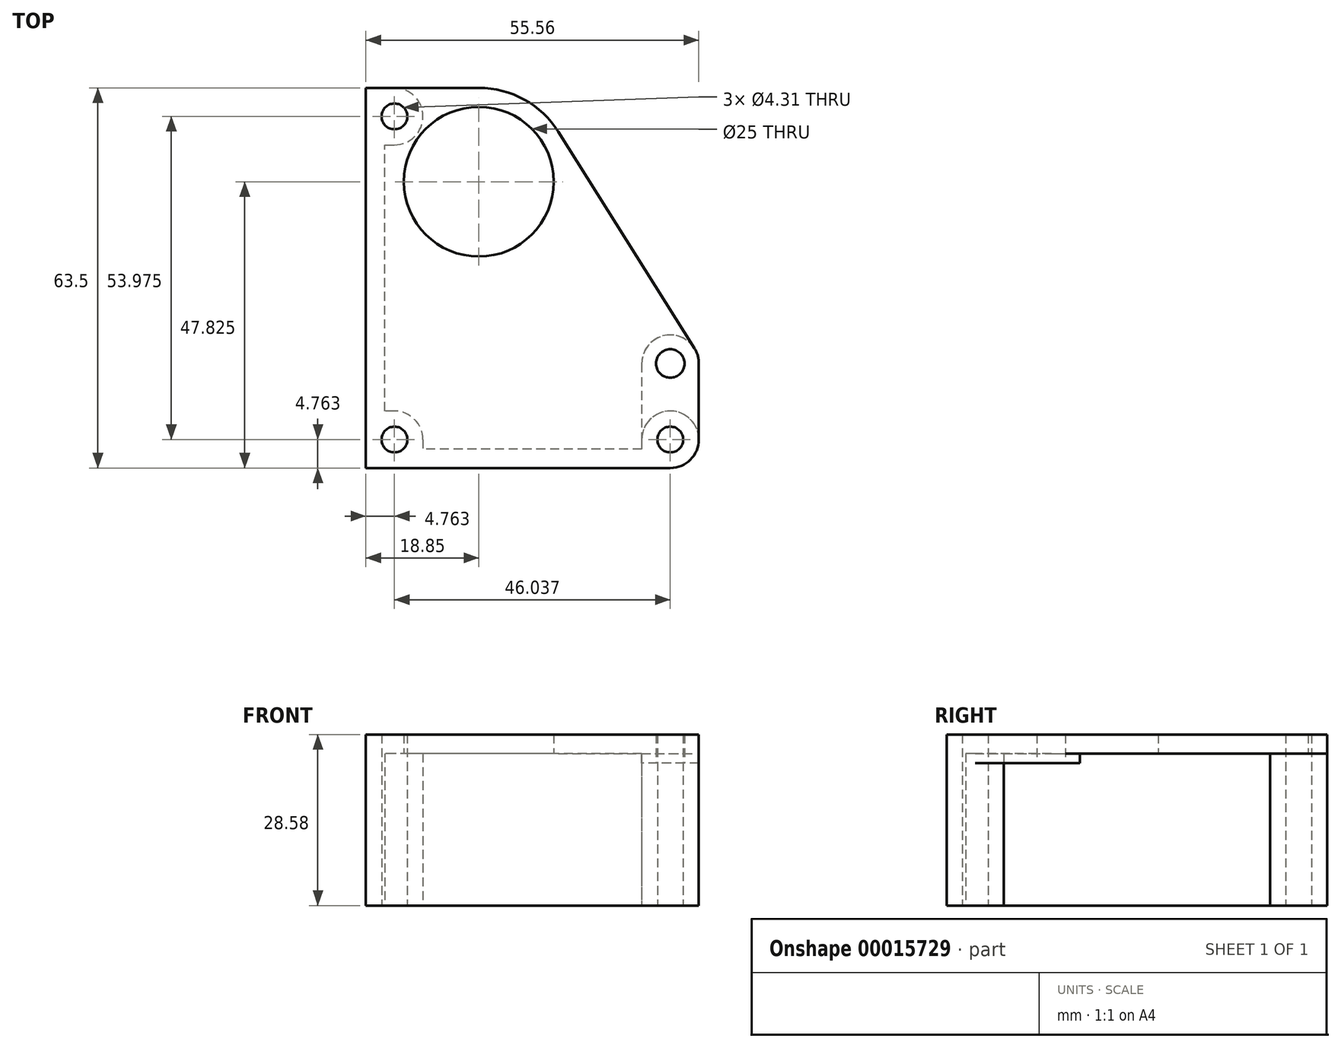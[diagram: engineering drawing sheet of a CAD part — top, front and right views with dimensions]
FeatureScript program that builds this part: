
annotation { "Feature Type Name" : "Feature", "Feature Type Description" : "" }
export const myFeature = defineFeature(function(context is Context, id is Id, definition is map)
    precondition{}
    {
        {
            var Q0;
            Q0=qCreatedBy(makeId("Top.planeOp"),FACE);
            var sketch = newSketch(context, id + "F0", { "sketchPlane" : qUnion([Q0])});
            skLineSegment(sketch, "E0.bottom", {"start": v(0, 0) * mm, "end": v(50.8, 0) * mm});
            skLineSegment(sketch, "E0.left", {"start": v(0, 0) * mm, "end": v(0, 63.5) * mm});
            skLineSegment(sketch, "E1", {"start": v(4.76, 0) * mm, "end": v(4.76, 4.76) * mm, "construction": true});
            skLineSegment(sketch, "E2", {"start": v(4.76, 4.76) * mm, "end": v(0, 4.76) * mm, "construction": true});
            skCircle(sketch, "E3", {"center": v(4.76, 4.76) * mm, "radius": 2.15 * mm});
            skCircle(sketch, "E4", {"center": v(50.8, 4.76) * mm, "radius": 2.15 * mm});
            skArc(sketch, "E5", {"start": v(50.8, 0) * mm, "mid": v(54.17, 8.13) * mm, "end": v(46.04, 4.76) * mm});
            skLineSegment(sketch, "E6", {"start": v(46.04, 4.76) * mm, "end": v(46.04, 3.18) * mm});
            skLineSegment(sketch, "E7", {"start": v(46.04, 3.18) * mm, "end": v(9.53, 3.17) * mm});
            skLineSegment(sketch, "E8", {"start": v(9.53, 4.76) * mm, "end": v(9.53, 3.17) * mm});
            skArc(sketch, "E9", {"start": v(9.53, 4.76) * mm, "mid": v(8.13, 8.13) * mm, "end": v(4.76, 9.52) * mm});
            skLineSegment(sketch, "E10", {"start": v(46.04, 3.18) * mm, "end": v(46.04, 0) * mm, "construction": true});
            skLineSegment(sketch, "E11", {"start": v(4.76, 9.52) * mm, "end": v(3.18, 9.52) * mm});
            skLineSegment(sketch, "E12", {"start": v(3.18, 9.52) * mm, "end": v(3.18, 53.98) * mm});
            skLineSegment(sketch, "E13", {"start": v(0, 63.5) * mm, "end": v(4.76, 63.5) * mm});
            skArc(sketch, "E14", {"start": v(4.76, 53.97) * mm, "mid": v(9.52, 58.74) * mm, "end": v(4.76, 63.5) * mm});
            skLineSegment(sketch, "E15", {"start": v(3.17, 53.98) * mm, "end": v(4.76, 53.98) * mm});
            skCircle(sketch, "E16", {"center": v(4.76, 58.74) * mm, "radius": 2.15 * mm});
            skLineSegment(sketch, "E17", {"start": v(50.8, 4.76) * mm, "end": v(50.8, 22.23) * mm, "construction": true});
            skLineSegment(sketch, "E18", {"start": v(4.76, 58.74) * mm, "end": v(23.08, 58.74) * mm, "construction": true});
            skLineSegment(sketch, "E19", {"start": v(23.08, 58.74) * mm, "end": v(23.08, 49.95) * mm, "construction": true});
            skLineSegment(sketch, "E20", {"start": v(23.08, 49.95) * mm, "end": v(50.8, 22.23) * mm, "construction": true});
            skSolve(sketch);
        }
        {
            var Q0;
            Q0 = qSketchRegion(id + "F0", true);
            extrude(context, id + "F1", {"entities" : qUnion([Q0]), "depth" : 25.4 * mm});
        }
        {
            var Q0;
            Q0=makeQuery(id+"F1.opExtrude","CAP_FACE",FACE,{"disambiguationData":[OSD([sQuery(id+"F0.wireOp",EDGE,"E0.bottom"),sQuery(id+"F0.wireOp",EDGE,"E0.left"),sQuery(id+"F0.wireOp",EDGE,"E3"),sQuery(id+"F0.wireOp",EDGE,"E4"),sQuery(id+"F0.wireOp",EDGE,"E5"),sQuery(id+"F0.wireOp",EDGE,"E6"),sQuery(id+"F0.wireOp",EDGE,"E7"),sQuery(id+"F0.wireOp",EDGE,"E8"),sQuery(id+"F0.wireOp",EDGE,"E9"),sQuery(id+"F0.wireOp",EDGE,"E11"),sQuery(id+"F0.wireOp",EDGE,"E12"),sQuery(id+"F0.wireOp",EDGE,"E13"),sQuery(id+"F0.wireOp",EDGE,"E14"),sQuery(id+"F0.wireOp",EDGE,"E15"),sQuery(id+"F0.wireOp",EDGE,"E16")])],"isStart":false});
            var sketch = newSketch(context, id + "F2", { "sketchPlane" : qUnion([Q0])});
            skLineSegment(sketch, "E21", {"start": v(55.56, 4.76) * mm, "end": v(55.56, 17.46) * mm});
            skLineSegment(sketch, "E22.bottom", {"start": v(50.8, 0) * mm, "end": v(0, 0) * mm});
            skLineSegment(sketch, "E22.top", {"start": v(18.85, 63.5) * mm, "end": v(0, 63.5) * mm});
            skLineSegment(sketch, "E22.right", {"start": v(0, 0) * mm, "end": v(0, 63.5) * mm});
            skArc(sketch, "E23", {"start": v(55.56, 17.46) * mm, "mid": v(55.38, 18.78) * mm, "end": v(54.83, 20) * mm});
            skArc(sketch, "E24", {"start": v(32.13, 56.16) * mm, "mid": v(26.43, 61.54) * mm, "end": v(18.85, 63.5) * mm});
            skCircle(sketch, "E25", {"center": v(18.85, 47.83) * mm, "radius": 12.5 * mm});
            skLineSegment(sketch, "E26", {"start": v(18.85, 47.83) * mm, "end": v(6.35, 47.83) * mm, "construction": true});
            skLineSegment(sketch, "E27", {"start": v(6.35, 47.83) * mm, "end": v(3.18, 47.83) * mm, "construction": true});
            skLineSegment(sketch, "E28", {"start": v(50.8, 4.76) * mm, "end": v(50.8, 17.46) * mm, "construction": true});
            skLineSegment(sketch, "E29", {"start": v(32.13, 56.16) * mm, "end": v(54.83, 20) * mm});
            skCircle(sketch, "E30", {"center": v(4.76, 58.74) * mm, "radius": 2.15 * mm});
            skCircle(sketch, "E31", {"center": v(50.8, 4.76) * mm, "radius": 2.15 * mm});
            skCircle(sketch, "E32", {"center": v(4.76, 4.76) * mm, "radius": 2.15 * mm});
            skCircle(sketch, "E33", {"center": v(50.8, 17.46) * mm, "radius": 2.38 * mm});
            skSolve(sketch);
        }
        {
            var Q0;
            {var subQ1=sQuery(id+"F2.wireOp",EDGE,"E21");Q0=makeQuery(id+"F2.imprint","IMPRINT",FACE,{"disambiguationData":[TD([[makeQuery(id+"F2.imprint","IMPRINT",EDGE,{"derivedFrom":subQ1}),1.0]])]});}
            var Q1;
            {var subQ0=sQuery(id+"F2.wireOp",EDGE,"E22.bottom");Q1=makeQuery(id+"F2.imprint","IMPRINT",FACE,{"disambiguationData":[TD([[makeQuery(id+"F2.imprint","IMPRINT",EDGE,{"derivedFrom":subQ0}),1.0]])]});}
            extrude(context, id + "F3", {"entities" : qUnion([Q0, Q1]), "operationType" : NewBodyOperationType.ADD, "depth" : 3.17 * mm});
        }
        {
            var Q0;
            Q0=makeQuery(id+"F3.opExtrude","CAP_FACE",FACE,{"disambiguationData":[OSD([sQuery(id+"F0.wireOp",EDGE,"E5"),sQuery(id+"F2.wireOp",EDGE,"E21"),sQuery(id+"F2.wireOp",EDGE,"E22.bottom"),sQuery(id+"F2.wireOp",EDGE,"E22.top"),sQuery(id+"F2.wireOp",EDGE,"E22.right"),sQuery(id+"F2.wireOp",EDGE,"E23"),sQuery(id+"F2.wireOp",EDGE,"E24"),sQuery(id+"F2.wireOp",EDGE,"E25"),sQuery(id+"F2.wireOp",EDGE,"E29"),sQuery(id+"F2.wireOp",EDGE,"E30"),sQuery(id+"F2.wireOp",EDGE,"E31"),sQuery(id+"F2.wireOp",EDGE,"E32"),sQuery(id+"F2.wireOp",EDGE,"E33")])],"isStart":true});
            var sketch = newSketch(context, id + "F4", { "sketchPlane" : qUnion([Q0])});
            skArc(sketch, "E34", {"start": v(46.04, -17.46) * mm, "mid": v(50.8, -22.23) * mm, "end": v(55.56, -17.46) * mm});
            skLineSegment(sketch, "E35", {"start": v(55.56, -4.76) * mm, "end": v(55.56, -17.46) * mm});
            skLineSegment(sketch, "E36", {"start": v(46.04, -17.46) * mm, "end": v(46.04, -4.76) * mm});
            skArc(sketch, "E37", {"start": v(46.04, -4.76) * mm, "mid": v(50.8, -9.53) * mm, "end": v(55.56, -4.76) * mm});
            skCircle(sketch, "E38", {"center": v(50.8, -17.46) * mm, "radius": 2.38 * mm});
            skSolve(sketch);
        }
        {
            var Q0;
            Q0 = qSketchRegion(id + "F4", true);
            extrude(context, id + "F5", {"entities" : qUnion([Q0]), "operationType" : NewBodyOperationType.ADD, "depth" : 1.59 * mm});
        }
    });
